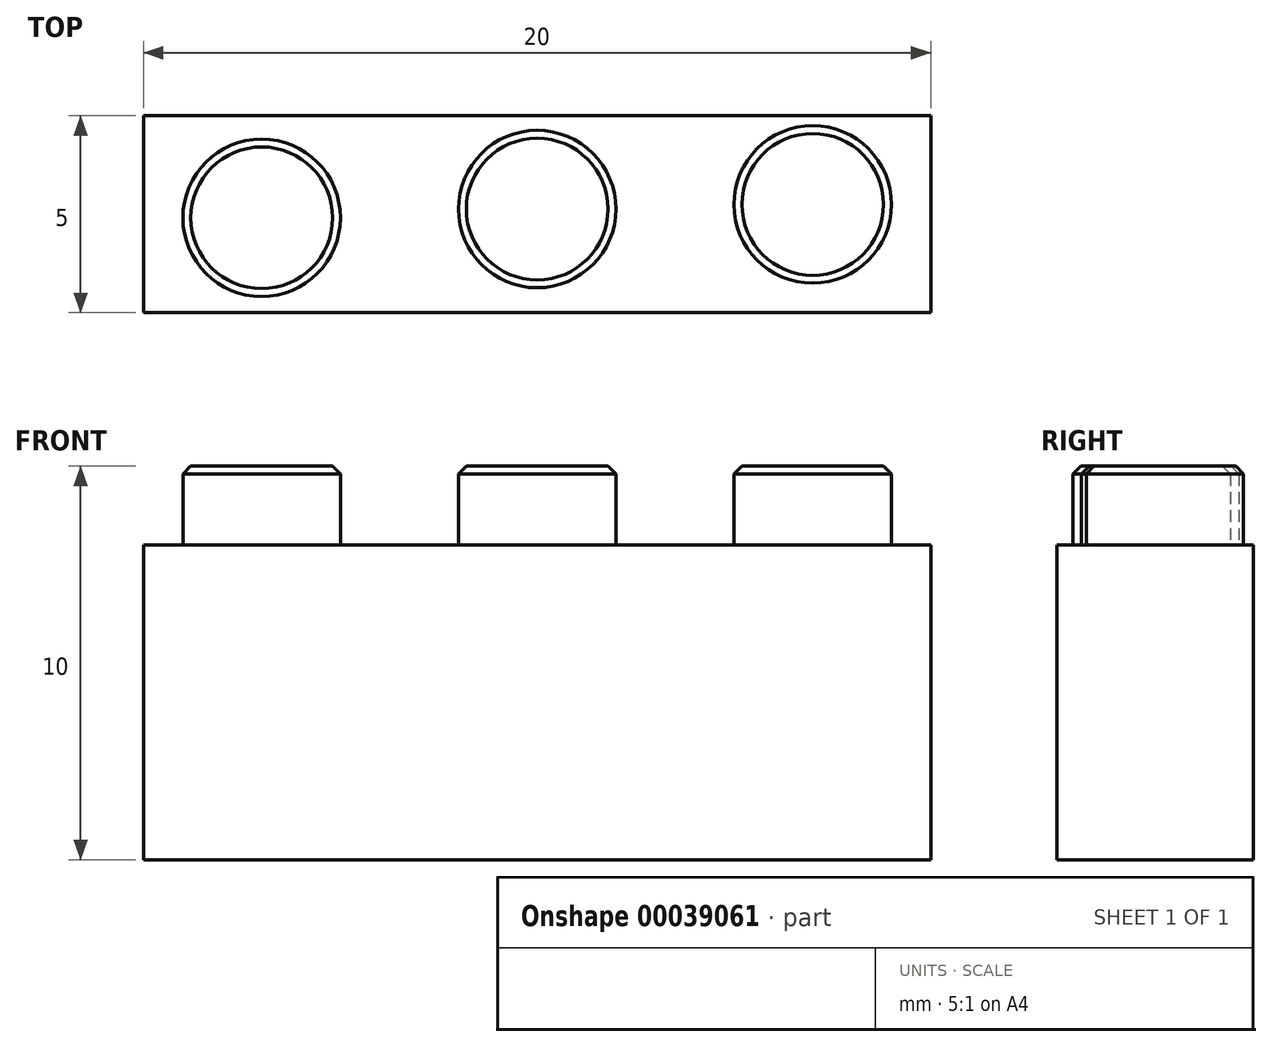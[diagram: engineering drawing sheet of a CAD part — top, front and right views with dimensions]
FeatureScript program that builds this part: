
annotation { "Feature Type Name" : "Feature", "Feature Type Description" : "" }
export const myFeature = defineFeature(function(context is Context, id is Id, definition is map)
    precondition{}
    {
        {
            var Q0;
            Q0=qCreatedBy(makeId("Top.planeOp"),FACE);
            var sketch = newSketch(context, id + "F0", { "sketchPlane" : qUnion([Q0])});
            skLineSegment(sketch, "E0.bottom", {"start": v(0, 0) * mm, "end": v(-20, 0) * mm});
            skLineSegment(sketch, "E0.top", {"start": v(0, 5) * mm, "end": v(-20, 5) * mm});
            skLineSegment(sketch, "E0.left", {"start": v(0, 0) * mm, "end": v(0, 5) * mm});
            skLineSegment(sketch, "E0.right", {"start": v(-20, 0) * mm, "end": v(-20, 5) * mm});
            skSolve(sketch);
        }
        {
            var Q0;
            Q0=makeQuery(id+"F0.imprint","IMPRINT",FACE,{"disambiguationData":[TD([[makeQuery(id+"F0.imprint","IMPRINT",EDGE,{"derivedFrom":sQuery(id+"F0.wireOp",EDGE,"E0.bottom")}),-1.0]])]});
            extrude(context, id + "F1", {"entities" : qUnion([Q0]), "depth" : 8 * mm});
        }
        {
            var Q0;
            Q0=makeQuery(id+"F1.opExtrude","CAP_FACE",FACE,{"disambiguationData":[OSD([sQuery(id+"F0.wireOp",EDGE,"E0.bottom"),sQuery(id+"F0.wireOp",EDGE,"E0.top"),sQuery(id+"F0.wireOp",EDGE,"E0.left"),sQuery(id+"F0.wireOp",EDGE,"E0.right")])],"isStart":false});
            var sketch = newSketch(context, id + "F2", { "sketchPlane" : qUnion([Q0])});
            skCircle(sketch, "E1", {"center": v(-17, 2.4) * mm, "radius": 2 * mm});
            skCircle(sketch, "E2", {"center": v(-10, 2.63) * mm, "radius": 2 * mm});
            skCircle(sketch, "E3", {"center": v(-3, 2.75) * mm, "radius": 2 * mm});
            skSolve(sketch);
        }
        {
            var Q0;
            Q0=makeQuery(id+"F2.imprint","IMPRINT",FACE,{"disambiguationData":[TD([[makeQuery(id+"F2.imprint","IMPRINT",EDGE,{"derivedFrom":sQuery(id+"F2.wireOp",EDGE,"E1")}),1.0]])]});
            var Q1;
            Q1=makeQuery(id+"F2.imprint","IMPRINT",FACE,{"disambiguationData":[TD([[makeQuery(id+"F2.imprint","IMPRINT",EDGE,{"derivedFrom":sQuery(id+"F2.wireOp",EDGE,"E2")}),1.0]])]});
            var Q2;
            Q2=makeQuery(id+"F2.imprint","IMPRINT",FACE,{"disambiguationData":[TD([[makeQuery(id+"F2.imprint","IMPRINT",EDGE,{"derivedFrom":sQuery(id+"F2.wireOp",EDGE,"E3")}),1.0]])]});
            extrude(context, id + "F3", {"entities" : qUnion([Q0, Q1, Q2]), "operationType" : NewBodyOperationType.ADD, "depth" : 2 * mm});
        }
        {
            var Q0;
            Q0=makeQuery(id+"F3.opExtrude","CAP_EDGE",EDGE,{"disambiguationData":[OSD([sQuery(id+"F2.wireOp",EDGE,"E1")])],"isStart":false});
            var Q1;
            Q1=makeQuery(id+"F3.opExtrude","CAP_EDGE",EDGE,{"disambiguationData":[OSD([sQuery(id+"F2.wireOp",EDGE,"E2")])],"isStart":false});
            var Q2;
            Q2=makeQuery(id+"F3.opExtrude","CAP_EDGE",EDGE,{"disambiguationData":[OSD([sQuery(id+"F2.wireOp",EDGE,"E3")])],"isStart":false});
            chamfer(context, id + "F4", {"entities" : qUnion([Q0, Q1, Q2]), "width" : 0.2 * mm, "tangentPropagation" : true});
        }
    });
